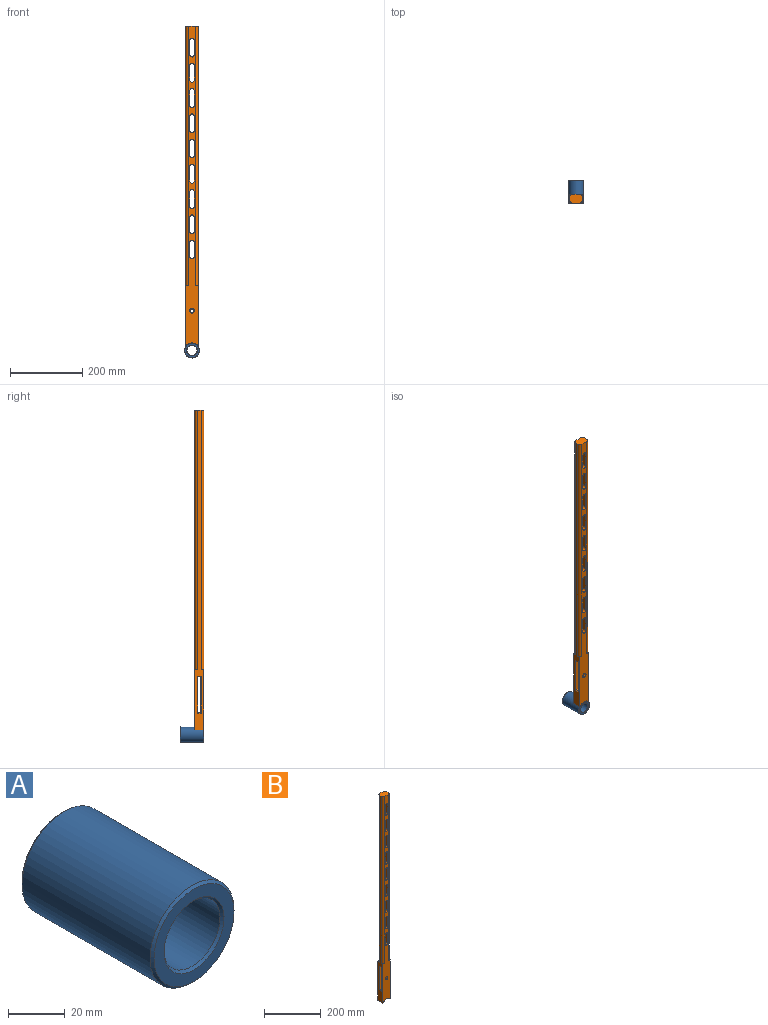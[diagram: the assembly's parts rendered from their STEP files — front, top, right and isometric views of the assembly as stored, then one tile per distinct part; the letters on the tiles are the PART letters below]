
ASSEMBLY  parts=2 mates=1
PART A: 8 faces, bbox 42x66x42 mm
  f0: cylinder r=14mm len=64mm, axis (0,1,0), area 5629.7mm2, adj f4,f7
  f1: cylinder r=21mm len=64mm, axis (0,1,0), area 8444.6mm2, adj f5,f6
  f2: plane 40x40mm, normal (0,-1,0), area 549.8mm2, adj f6,f7
  f3: plane 40x40mm, normal (0,1,0), area 549.8mm2, adj f4,f5
  f4: cone r=15mm half-angle=45deg, axis (0,1,0), area 128.8mm2, adj f0,f3
  f5: cone r=21mm half-angle=45deg, axis (0,-1,0), area 182.2mm2, adj f1,f3
  f6: cone r=20mm half-angle=45deg, axis (0,1,0), area 182.2mm2, adj f1,f2
  f7: cone r=14mm half-angle=45deg, axis (0,-1,0), area 128.8mm2, adj f0,f2
PART B: 66 faces, bbox 35x25x888.4 mm
  f0: plane 888.39x35mm, normal (0,-1,0), area 13871.8mm2, adj f2,f3,f5,f6,f13,f26,f27,f28
  f1: plane 888.39x35mm, normal (0,1,0), area 13871.8mm2, adj f2,f3,f5,f6,f12,f22,f23,f24
  f2: plane 888.39x25mm, normal (1,0,0), area 9618.8mm2, adj f0,f1,f5,f6,f18,f19,f20,f21
  f3: plane 888.39x25mm, normal (-1,0,0), area 9618.8mm2, adj f0,f1,f5,f6,f14,f15,f16,f17
  f4: cylinder r=5.5mm len=11mm, axis (0,-1,0), area 250.5mm2, adj f9,f13
  f5: plane 35x25mm, normal (0,0,1), area 820.1mm2, adj f0,f1,f2,f3,f22,f24,f26,f28
  f6: cylinder r=21mm len=35mm, axis (0,-1,0), area 1034.4mm2, adj f0,f1,f2,f3
  f7: cylinder r=5.5mm len=11mm, axis (0,-1,0), area 250.5mm2, adj f8,f12
  f8: plane 100x33mm, normal (0,-1,0), area 3205mm2, adj f7,f10,f11,f16,f21
  f9: plane 100x33mm, normal (0,1,0), area 3205mm2, adj f4,f10,f11,f15,f18
  f10: plane 33x8.5mm, normal (0,0,1), area 280.5mm2, adj f8,f9,f17,f19
  f11: plane 33x8.5mm, normal (0,0,-1), area 280.5mm2, adj f8,f9,f14,f20
  f12: cone r=6.5mm half-angle=45deg, axis (0,1,0), area 53.3mm2, adj f1,f7
  f13: cone r=5.5mm half-angle=45deg, axis (0,-1,0), area 53.3mm2, adj f0,f4
  f14: plane 10.5x1mm, normal (-0.71,0,-0.71), area 13.4mm2, adj f3,f11,f15,f16
  f15: plane 102x1mm, normal (-0.71,0.71,0), area 142.8mm2, adj f3,f9,f14,f17
  f16: plane 102x1mm, normal (-0.71,-0.71,0), area 142.8mm2, adj f3,f8,f14,f17
  f17: plane 10.5x1mm, normal (-0.71,0,0.71), area 13.4mm2, adj f3,f10,f15,f16
  f18: plane 102x1mm, normal (0.71,0.71,0), area 142.8mm2, adj f2,f9,f19,f20
  f19: plane 10.5x1mm, normal (0.71,0,0.71), area 13.4mm2, adj f2,f10,f18,f21
  f20: plane 10.5x1mm, normal (0.71,0,-0.71), area 13.4mm2, adj f2,f11,f18,f21
  f21: plane 102x1mm, normal (0.71,-0.71,0), area 142.8mm2, adj f2,f8,f19,f20
  f22: cylinder r=8mm len=720mm, axis (0,0,1), area 9047.8mm2, adj f1,f3,f5,f23
  f23: plane 8x8mm, normal (0,0,1), area 13.7mm2, adj f1,f3,f22
  f24: cylinder r=8mm len=720mm, axis (0,0,1), area 9047.8mm2, adj f1,f2,f5,f25
  f25: plane 8x8mm, normal (0,0,1), area 13.7mm2, adj f1,f2,f24
  f26: cylinder r=8mm len=720mm, axis (0,0,1), area 9047.8mm2, adj f0,f3,f5,f27
  f27: plane 8x8mm, normal (0,0,1), area 13.7mm2, adj f0,f3,f26
  f28: cylinder r=8mm len=720mm, axis (0,0,1), area 9047.8mm2, adj f0,f2,f5,f29
  f29: plane 8x8mm, normal (0,0,1), area 13.7mm2, adj f0,f2,f28
  f30: cylinder r=6mm len=25mm, axis (0,1,0), area 471.2mm2, adj f0,f1,f31,f33
  f31: plane 40x25mm, normal (-1,0,0), area 1000mm2, adj f0,f1,f30,f32
  f32: cylinder r=6mm len=25mm, axis (0,1,0), area 471.2mm2, adj f0,f1,f31,f33
  f33: plane 40x25mm, normal (1,0,0), area 1000mm2, adj f0,f1,f30,f32
  f34: cylinder r=6mm len=25mm, axis (0,1,0), area 471.2mm2, adj f0,f1,f35,f37
  f35: plane 40x25mm, normal (-1,0,0), area 1000mm2, adj f0,f1,f34,f36
  f36: cylinder r=6mm len=25mm, axis (0,1,0), area 471.2mm2, adj f0,f1,f35,f37
  f37: plane 40x25mm, normal (1,0,0), area 1000mm2, adj f0,f1,f34,f36
  f38: cylinder r=6mm len=25mm, axis (0,1,0), area 471.2mm2, adj f0,f1,f39,f41
  f39: plane 40x25mm, normal (-1,0,0), area 1000mm2, adj f0,f1,f38,f40
  f40: cylinder r=6mm len=25mm, axis (0,1,0), area 471.2mm2, adj f0,f1,f39,f41
  f41: plane 40x25mm, normal (1,0,0), area 1000mm2, adj f0,f1,f38,f40
  f42: cylinder r=6mm len=25mm, axis (0,1,0), area 471.2mm2, adj f0,f1,f43,f45
  f43: plane 40x25mm, normal (-1,0,0), area 1000mm2, adj f0,f1,f42,f44
  f44: cylinder r=6mm len=25mm, axis (0,1,0), area 471.2mm2, adj f0,f1,f43,f45
  f45: plane 40x25mm, normal (1,0,0), area 1000mm2, adj f0,f1,f42,f44
  f46: cylinder r=6mm len=25mm, axis (0,1,0), area 471.2mm2, adj f0,f1,f47,f49
  f47: plane 40x25mm, normal (-1,0,0), area 1000mm2, adj f0,f1,f46,f48
  f48: cylinder r=6mm len=25mm, axis (0,1,0), area 471.2mm2, adj f0,f1,f47,f49
  f49: plane 40x25mm, normal (1,0,0), area 1000mm2, adj f0,f1,f46,f48
  f50: cylinder r=6mm len=25mm, axis (0,1,0), area 471.2mm2, adj f0,f1,f51,f53
  f51: plane 40x25mm, normal (-1,0,0), area 1000mm2, adj f0,f1,f50,f52
  f52: cylinder r=6mm len=25mm, axis (0,1,0), area 471.2mm2, adj f0,f1,f51,f53
  f53: plane 40x25mm, normal (1,0,0), area 1000mm2, adj f0,f1,f50,f52
  f54: cylinder r=6mm len=25mm, axis (0,1,0), area 471.2mm2, adj f0,f1,f55,f57
  f55: plane 40x25mm, normal (-1,0,0), area 1000mm2, adj f0,f1,f54,f56
  f56: cylinder r=6mm len=25mm, axis (0,1,0), area 471.2mm2, adj f0,f1,f55,f57
  f57: plane 40x25mm, normal (1,0,0), area 1000mm2, adj f0,f1,f54,f56
  f58: cylinder r=6mm len=25mm, axis (0,1,0), area 471.2mm2, adj f0,f1,f59,f61
  f59: plane 40x25mm, normal (-1,0,0), area 1000mm2, adj f0,f1,f58,f60
  f60: cylinder r=6mm len=25mm, axis (0,1,0), area 471.2mm2, adj f0,f1,f59,f61
  f61: plane 40x25mm, normal (1,0,0), area 1000mm2, adj f0,f1,f58,f60
  f62: plane 40x25mm, normal (1,0,0), area 1000mm2, adj f0,f1,f63,f65
  f63: cylinder r=6mm len=25mm, axis (0,1,0), area 471.2mm2, adj f0,f1,f62,f64
  f64: plane 40x25mm, normal (-1,0,0), area 1000mm2, adj f0,f1,f63,f65
  f65: cylinder r=6mm len=25mm, axis (0,1,0), area 471.2mm2, adj f0,f1,f62,f64
PLACE A at identity
PLACE B t=(17.5,-53.5,11.61)mm
MATE fastened B.f6 <-> A.f1  axis (0,-1,0) through (0,-66,0)mm
